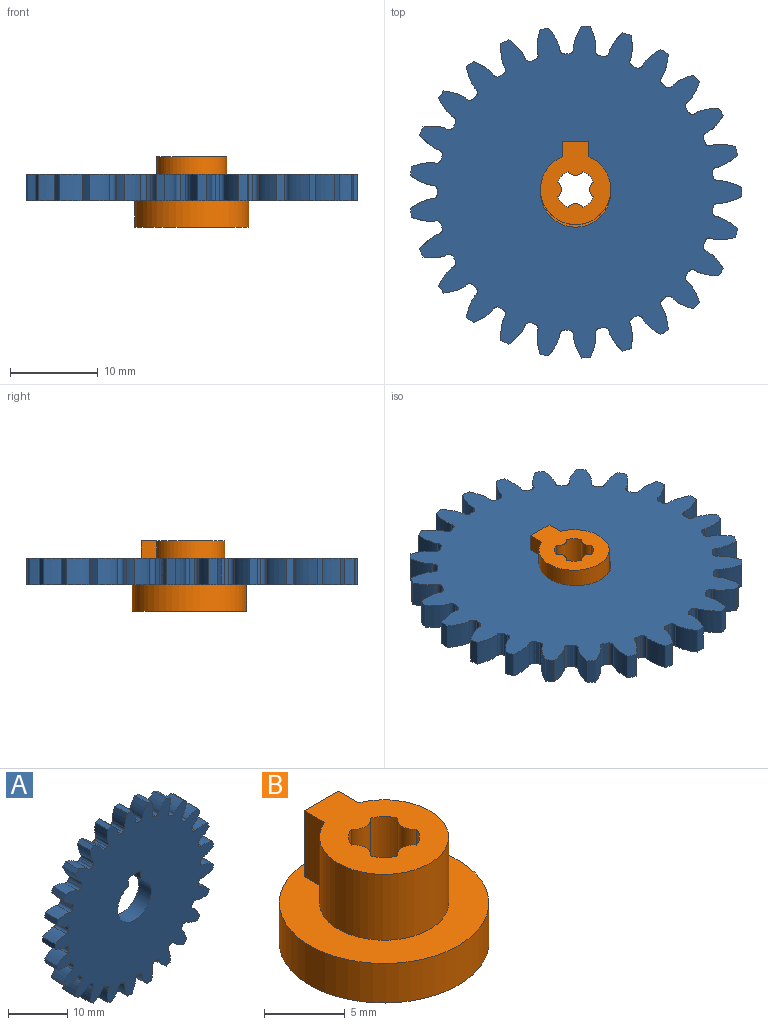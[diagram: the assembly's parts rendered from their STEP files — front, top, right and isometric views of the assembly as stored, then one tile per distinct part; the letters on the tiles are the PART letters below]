
ASSEMBLY  parts=2 mates=1
PART A: 156 faces, bbox 37.7x3x37.8 mm
  f0: cylinder r=18.9mm len=3mm, axis (0,1,0), area 3mm2, adj f24,f30,f141,f153
  f1: cylinder r=18.9mm len=3mm, axis (0,1,0), area 3mm2, adj f24,f30,f148,f151
  f2: cylinder r=18.9mm len=3mm, axis (0,1,0), area 3mm2, adj f24,f30,f136,f143
  f3: cylinder r=18.9mm len=3mm, axis (0,1,0), area 3mm2, adj f24,f30,f131,f138
  f4: cylinder r=18.9mm len=3mm, axis (0,1,0), area 3mm2, adj f24,f30,f126,f133
  f5: cylinder r=18.9mm len=3mm, axis (0,1,0), area 3mm2, adj f24,f30,f116,f128
  f6: cylinder r=18.9mm len=3mm, axis (0,1,0), area 3mm2, adj f24,f30,f111,f123
  f7: cylinder r=18.9mm len=3mm, axis (0,1,0), area 3mm2, adj f24,f30,f118,f121
  f8: cylinder r=18.9mm len=3mm, axis (0,1,0), area 3mm2, adj f24,f30,f106,f113
  f9: cylinder r=18.9mm len=3mm, axis (0,1,0), area 3mm2, adj f24,f30,f101,f108
  f10: cylinder r=18.9mm len=3mm, axis (0,1,0), area 3mm2, adj f24,f30,f96,f103
  f11: cylinder r=18.9mm len=3mm, axis (0,1,0), area 3mm2, adj f24,f30,f81,f98
  f12: cylinder r=18.9mm len=3mm, axis (0,1,0), area 3mm2, adj f24,f30,f31,f93
  f13: cylinder r=18.9mm len=3mm, axis (0,1,0), area 3mm2, adj f24,f30,f88,f91
  f14: cylinder r=18.9mm len=3mm, axis (0,1,0), area 3mm2, adj f24,f30,f76,f83
  f15: cylinder r=18.9mm len=3mm, axis (0,1,0), area 3mm2, adj f24,f30,f78,f86
  f16: cylinder r=18.9mm len=3mm, axis (0,1,0), area 3mm2, adj f24,f30,f73,f146
  f17: cylinder r=18.9mm len=3mm, axis (0,1,0), area 3mm2, adj f24,f30,f68,f71
  f18: cylinder r=18.9mm len=3mm, axis (0,1,0), area 3mm2, adj f24,f30,f63,f66
  f19: cylinder r=18.9mm len=3mm, axis (0,1,0), area 3mm2, adj f24,f30,f58,f61
  f20: cylinder r=18.9mm len=3mm, axis (0,1,0), area 3mm2, adj f24,f30,f46,f53
  f21: cylinder r=18.9mm len=3mm, axis (0,1,0), area 3mm2, adj f24,f30,f36,f48
  f22: cylinder r=18.9mm len=3mm, axis (0,1,0), area 3mm2, adj f24,f30,f43,f56
  f23: cylinder r=18.9mm len=3mm, axis (0,1,0), area 3mm2, adj f24,f30,f38,f41
  f24: plane 37.78x37.71mm, normal (0,-1,0), area 892.9mm2, adj f0,f1,f2,f3,f4,f5,f6,f7
  f25: plane 3x1.79mm, normal (-1,0,0), area 5.4mm2, adj f24,f26,f28,f30
  f26: cylinder r=4mm len=8mm, axis (0,1,0), area 66.2mm2, adj f24,f25,f27,f30
  f27: plane 3x1.79mm, normal (1,0,0), area 5.4mm2, adj f24,f26,f28,f30
  f28: plane 3x3mm, normal (0,0,-1), area 9mm2, adj f24,f25,f27,f30
  f29: cylinder r=18.9mm len=3mm, axis (0,1,0), area 3mm2, adj f24,f30,f33,f51
  f30: plane 37.78x37.71mm, normal (0,1,0), area 892.9mm2, adj f0,f1,f2,f3,f4,f5,f6,f7
  f31: extruded ~3x2.56mm, area 8.4mm2, adj f12,f24,f30,f34
  f32: cylinder r=15.75mm len=3mm, axis (0,1,0), area 1.4mm2, adj f24,f30,f34,f35
  f33: extruded ~3x2.56mm, area 8.4mm2, adj f24,f29,f30,f35
  f34: cylinder r=0.53mm len=3mm, axis (0,1,0), area 2.4mm2, adj f24,f30,f31,f32
  f35: cylinder r=0.53mm len=3mm, axis (0,1,0), area 2.4mm2, adj f24,f30,f32,f33
  f36: extruded ~3x2.61mm, area 8.4mm2, adj f21,f24,f30,f39
  f37: cylinder r=15.75mm len=3mm, axis (0,1,0), area 1.4mm2, adj f24,f30,f39,f40
  f38: extruded ~3x2.54mm, area 8.4mm2, adj f23,f24,f30,f40
  f39: cylinder r=0.53mm len=3mm, axis (0,1,0), area 2.4mm2, adj f24,f30,f36,f37
  f40: cylinder r=0.53mm len=3mm, axis (0,1,0), area 2.4mm2, adj f24,f30,f37,f38
  f41: extruded ~3x2.29mm, area 8.4mm2, adj f23,f24,f30,f44
  f42: cylinder r=15.75mm len=3mm, axis (0,1,0), area 1.4mm2, adj f24,f30,f44,f45
  f43: extruded ~3x2.74mm, area 8.4mm2, adj f22,f24,f30,f45
  f44: cylinder r=0.53mm len=3mm, axis (0,1,0), area 2.4mm2, adj f24,f30,f41,f42
  f45: cylinder r=0.53mm len=3mm, axis (0,1,0), area 2.4mm2, adj f24,f30,f42,f43
  f46: extruded ~3x2.77mm, area 8.4mm2, adj f20,f24,f30,f49
  f47: cylinder r=15.75mm len=3mm, axis (0,1,0), area 1.4mm2, adj f24,f30,f49,f50
  f48: extruded ~3x2.19mm, area 8.4mm2, adj f21,f24,f30,f50
  f49: cylinder r=0.53mm len=3mm, axis (0,1,0), area 2.4mm2, adj f24,f30,f46,f47
  f50: cylinder r=0.53mm len=3mm, axis (0,1,0), area 2.4mm2, adj f24,f30,f47,f48
  f51: extruded ~3x2.75mm, area 8.4mm2, adj f24,f29,f30,f54
  f52: cylinder r=15.75mm len=3mm, axis (0,1,0), area 1.4mm2, adj f24,f30,f54,f55
  f53: extruded ~3x2.2mm, area 8.4mm2, adj f20,f24,f30,f55
  f54: cylinder r=0.53mm len=3mm, axis (0,1,0), area 2.4mm2, adj f24,f30,f51,f52
  f55: cylinder r=0.53mm len=3mm, axis (0,1,0), area 2.4mm2, adj f24,f30,f52,f53
  f56: extruded ~3x2.09mm, area 8.4mm2, adj f22,f24,f30,f59
  f57: cylinder r=15.75mm len=3mm, axis (0,1,0), area 1.4mm2, adj f24,f30,f59,f60
  f58: extruded ~3x2.77mm, area 8.4mm2, adj f19,f24,f30,f60
  f59: cylinder r=0.53mm len=3mm, axis (0,1,0), area 2.4mm2, adj f24,f30,f56,f57
  f60: cylinder r=0.53mm len=3mm, axis (0,1,0), area 2.4mm2, adj f24,f30,f57,f58
  f61: extruded ~3x2.48mm, area 8.4mm2, adj f19,f24,f30,f64
  f62: cylinder r=15.75mm len=3mm, axis (0,1,0), area 1.4mm2, adj f24,f30,f64,f65
  f63: extruded ~3x2.62mm, area 8.4mm2, adj f18,f24,f30,f65
  f64: cylinder r=0.53mm len=3mm, axis (0,1,0), area 2.4mm2, adj f24,f30,f61,f62
  f65: cylinder r=0.53mm len=3mm, axis (0,1,0), area 2.4mm2, adj f24,f30,f62,f63
  f66: extruded ~3x2.71mm, area 8.4mm2, adj f18,f24,f30,f69
  f67: cylinder r=15.75mm len=3mm, axis (0,1,0), area 1.4mm2, adj f24,f30,f69,f70
  f68: extruded ~3x2.31mm, area 8.4mm2, adj f17,f24,f30,f70
  f69: cylinder r=0.53mm len=3mm, axis (0,1,0), area 2.4mm2, adj f24,f30,f66,f67
  f70: cylinder r=0.53mm len=3mm, axis (0,1,0), area 2.4mm2, adj f24,f30,f67,f68
  f71: extruded ~3x2.78mm, area 8.4mm2, adj f17,f24,f30,f74
  f72: cylinder r=15.75mm len=3mm, axis (0,1,0), area 1.4mm2, adj f24,f30,f74,f75
  f73: extruded ~3x2.08mm, area 8.4mm2, adj f16,f24,f30,f75
  f74: cylinder r=0.53mm len=3mm, axis (0,1,0), area 2.4mm2, adj f24,f30,f71,f72
  f75: cylinder r=0.53mm len=3mm, axis (0,1,0), area 2.4mm2, adj f24,f30,f72,f73
  f76: extruded ~3x2.54mm, area 8.4mm2, adj f14,f24,f30,f79
  f77: cylinder r=15.75mm len=3mm, axis (0,1,0), area 1.4mm2, adj f24,f30,f79,f80
  f78: extruded ~3x2.61mm, area 8.4mm2, adj f15,f24,f30,f80
  f79: cylinder r=0.53mm len=3mm, axis (0,1,0), area 2.4mm2, adj f24,f30,f76,f77
  f80: cylinder r=0.53mm len=3mm, axis (0,1,0), area 2.4mm2, adj f24,f30,f77,f78
  f81: extruded ~3x2.74mm, area 8.4mm2, adj f11,f24,f30,f84
  f82: cylinder r=15.75mm len=3mm, axis (0,1,0), area 1.4mm2, adj f24,f30,f84,f85
  f83: extruded ~3x2.29mm, area 8.4mm2, adj f14,f24,f30,f85
  f84: cylinder r=0.53mm len=3mm, axis (0,1,0), area 2.4mm2, adj f24,f30,f81,f82
  f85: cylinder r=0.53mm len=3mm, axis (0,1,0), area 2.4mm2, adj f24,f30,f82,f83
  f86: extruded ~3x2.19mm, area 8.4mm2, adj f15,f24,f30,f89
  f87: cylinder r=15.75mm len=3mm, axis (0,1,0), area 1.4mm2, adj f24,f30,f89,f90
  f88: extruded ~3x2.77mm, area 8.4mm2, adj f13,f24,f30,f90
  f89: cylinder r=0.53mm len=3mm, axis (0,1,0), area 2.4mm2, adj f24,f30,f86,f87
  f90: cylinder r=0.53mm len=3mm, axis (0,1,0), area 2.4mm2, adj f24,f30,f87,f88
  f91: extruded ~3x2.2mm, area 8.4mm2, adj f13,f24,f30,f94
  f92: cylinder r=15.75mm len=3mm, axis (0,1,0), area 1.4mm2, adj f24,f30,f94,f95
  f93: extruded ~3x2.75mm, area 8.4mm2, adj f12,f24,f30,f95
  f94: cylinder r=0.53mm len=3mm, axis (0,1,0), area 2.4mm2, adj f24,f30,f91,f92
  f95: cylinder r=0.53mm len=3mm, axis (0,1,0), area 2.4mm2, adj f24,f30,f92,f93
  f96: extruded ~3x2.77mm, area 8.4mm2, adj f10,f24,f30,f99
  f97: cylinder r=15.75mm len=3mm, axis (0,1,0), area 1.4mm2, adj f24,f30,f99,f100
  f98: extruded ~3x2.09mm, area 8.4mm2, adj f11,f24,f30,f100
  f99: cylinder r=0.53mm len=3mm, axis (0,1,0), area 2.4mm2, adj f24,f30,f96,f97
  f100: cylinder r=0.53mm len=3mm, axis (0,1,0), area 2.4mm2, adj f24,f30,f97,f98
  f101: extruded ~3x2.62mm, area 8.4mm2, adj f9,f24,f30,f104
  f102: cylinder r=15.75mm len=3mm, axis (0,1,0), area 1.4mm2, adj f24,f30,f104,f105
  f103: extruded ~3x2.48mm, area 8.4mm2, adj f10,f24,f30,f105
  f104: cylinder r=0.53mm len=3mm, axis (0,1,0), area 2.4mm2, adj f24,f30,f101,f102
  f105: cylinder r=0.53mm len=3mm, axis (0,1,0), area 2.4mm2, adj f24,f30,f102,f103
  f106: extruded ~3x2.31mm, area 8.4mm2, adj f8,f24,f30,f109
  f107: cylinder r=15.75mm len=3mm, axis (0,1,0), area 1.4mm2, adj f24,f30,f109,f110
  f108: extruded ~3x2.71mm, area 8.4mm2, adj f9,f24,f30,f110
  f109: cylinder r=0.53mm len=3mm, axis (0,1,0), area 2.4mm2, adj f24,f30,f106,f107
  f110: cylinder r=0.53mm len=3mm, axis (0,1,0), area 2.4mm2, adj f24,f30,f107,f108
  f111: extruded ~3x2.08mm, area 8.4mm2, adj f6,f24,f30,f114
  f112: cylinder r=15.75mm len=3mm, axis (0,1,0), area 1.4mm2, adj f24,f30,f114,f115
  f113: extruded ~3x2.78mm, area 8.4mm2, adj f8,f24,f30,f115
  f114: cylinder r=0.53mm len=3mm, axis (0,1,0), area 2.4mm2, adj f24,f30,f111,f112
  f115: cylinder r=0.53mm len=3mm, axis (0,1,0), area 2.4mm2, adj f24,f30,f112,f113
  f116: extruded ~3x2.71mm, area 8.4mm2, adj f5,f24,f30,f119
  f117: cylinder r=15.75mm len=3mm, axis (0,1,0), area 1.4mm2, adj f24,f30,f119,f120
  f118: extruded ~3x2.38mm, area 8.4mm2, adj f7,f24,f30,f120
  f119: cylinder r=0.53mm len=3mm, axis (0,1,0), area 2.4mm2, adj f24,f30,f116,f117
  f120: cylinder r=0.53mm len=3mm, axis (0,1,0), area 2.4mm2, adj f24,f30,f117,f118
  f121: extruded ~3x2.47mm, area 8.4mm2, adj f7,f24,f30,f124
  f122: cylinder r=15.75mm len=3mm, axis (0,1,0), area 1.4mm2, adj f24,f30,f124,f125
  f123: extruded ~3x2.66mm, area 8.4mm2, adj f6,f24,f30,f125
  f124: cylinder r=0.53mm len=3mm, axis (0,1,0), area 2.4mm2, adj f24,f30,f121,f122
  f125: cylinder r=0.53mm len=3mm, axis (0,1,0), area 2.4mm2, adj f24,f30,f122,f123
  f126: extruded ~3x2.78mm, area 8.4mm2, adj f4,f24,f30,f129
  f127: cylinder r=15.75mm len=3mm, axis (0,1,0), area 1.4mm2, adj f24,f30,f129,f130
  f128: extruded ~3x1.97mm, area 8.4mm2, adj f5,f24,f30,f130
  f129: cylinder r=0.53mm len=3mm, axis (0,1,0), area 2.4mm2, adj f24,f30,f126,f127
  f130: cylinder r=0.53mm len=3mm, axis (0,1,0), area 2.4mm2, adj f24,f30,f127,f128
  f131: extruded ~3x2.67mm, area 8.4mm2, adj f3,f24,f30,f134
  f132: cylinder r=15.75mm len=3mm, axis (0,1,0), area 1.4mm2, adj f24,f30,f134,f135
  f133: extruded ~3x2.4mm, area 8.4mm2, adj f4,f24,f30,f135
  f134: cylinder r=0.53mm len=3mm, axis (0,1,0), area 2.4mm2, adj f24,f30,f131,f132
  f135: cylinder r=0.53mm len=3mm, axis (0,1,0), area 2.4mm2, adj f24,f30,f132,f133
  f136: extruded ~3x2.4mm, area 8.4mm2, adj f2,f24,f30,f139
  f137: cylinder r=15.75mm len=3mm, axis (0,1,0), area 1.4mm2, adj f24,f30,f139,f140
  f138: extruded ~3x2.67mm, area 8.4mm2, adj f3,f24,f30,f140
  f139: cylinder r=0.53mm len=3mm, axis (0,1,0), area 2.4mm2, adj f24,f30,f136,f137
  f140: cylinder r=0.53mm len=3mm, axis (0,1,0), area 2.4mm2, adj f24,f30,f137,f138
  f141: extruded ~3x1.97mm, area 8.4mm2, adj f0,f24,f30,f144
  f142: cylinder r=15.75mm len=3mm, axis (0,1,0), area 1.4mm2, adj f24,f30,f144,f145
  f143: extruded ~3x2.78mm, area 8.4mm2, adj f2,f24,f30,f145
  f144: cylinder r=0.53mm len=3mm, axis (0,1,0), area 2.4mm2, adj f24,f30,f141,f142
  f145: cylinder r=0.53mm len=3mm, axis (0,1,0), area 2.4mm2, adj f24,f30,f142,f143
  f146: extruded ~3x2.66mm, area 8.4mm2, adj f16,f24,f30,f149
  f147: cylinder r=15.75mm len=3mm, axis (0,1,0), area 1.4mm2, adj f24,f30,f149,f150
  f148: extruded ~3x2.47mm, area 8.4mm2, adj f1,f24,f30,f150
  f149: cylinder r=0.53mm len=3mm, axis (0,1,0), area 2.4mm2, adj f24,f30,f146,f147
  f150: cylinder r=0.53mm len=3mm, axis (0,1,0), area 2.4mm2, adj f24,f30,f147,f148
  f151: extruded ~3x2.38mm, area 8.4mm2, adj f1,f24,f30,f154
  f152: cylinder r=15.75mm len=3mm, axis (0,1,0), area 1.4mm2, adj f24,f30,f154,f155
  f153: extruded ~3x2.71mm, area 8.4mm2, adj f0,f24,f30,f155
  f154: cylinder r=0.53mm len=3mm, axis (0,1,0), area 2.4mm2, adj f24,f30,f151,f152
  f155: cylinder r=0.53mm len=3mm, axis (0,1,0), area 2.4mm2, adj f24,f30,f152,f153
PART B: 18 faces, bbox 13x13x8 mm
  f0: cylinder r=2.2mm len=6mm, axis (0,0,-1), area 10.6mm2, adj f11,f13,f14,f17
  f1: cylinder r=2.2mm len=6mm, axis (0,0,-1), area 10.6mm2, adj f11,f13,f16,f17
  f2: cylinder r=2.2mm len=6mm, axis (0,0,-1), area 10.6mm2, adj f11,f13,f15,f16
  f3: cylinder r=2.2mm len=6mm, axis (0,0,-1), area 10.6mm2, adj f11,f13,f14,f15
  f4: cylinder r=6.5mm len=13mm, axis (0,0,-1), area 122.5mm2, adj f5,f6
  f5: plane 13x13mm, normal (0,0,1), area 77.7mm2, adj f4,f7,f8,f9,f10
  f6: plane 13x13mm, normal (0,0,-1), area 99.5mm2, adj f4,f12
  f7: cylinder r=4mm len=8mm, axis (0,0,-1), area 110.3mm2, adj f5,f8,f10,f11
  f8: plane 5x1.79mm, normal (1,0,0), area 9mm2, adj f5,f7,f9,f11
  f9: plane 5x3mm, normal (0,1,0), area 15mm2, adj f5,f8,f10,f11
  f10: plane 5x1.79mm, normal (-1,0,0), area 9mm2, adj f5,f7,f9,f11
  f11: plane 9.5x8mm, normal (0,0,1), area 42.6mm2, adj f0,f1,f2,f3,f7,f8,f9,f10
  f12: cylinder r=3.25mm len=6.5mm, axis (0,0,1), area 40.8mm2, adj f6,f13
  f13: plane 6.5x6.5mm, normal (0,0,-1), area 20.7mm2, adj f0,f1,f2,f3,f12,f14,f15,f16
  f14: cylinder r=1mm len=6mm, axis (0,0,1), area 11.7mm2, adj f0,f3,f11,f13
  f15: cylinder r=1mm len=6mm, axis (0,0,1), area 11.7mm2, adj f2,f3,f11,f13
  f16: cylinder r=1mm len=6mm, axis (0,0,1), area 11.7mm2, adj f1,f2,f11,f13
  f17: cylinder r=1mm len=6mm, axis (0,0,1), area 11.7mm2, adj f0,f1,f11,f13
PLACE A rot(axis=(0,0.71,0.71),180deg) t=(10.96,11.65,10.41)mm
PLACE B t=(10.96,11.94,-9.59)mm
MATE fastened A.f0 <-> B.f5  axis (0,0,-1) through (10.96,11.65,7.41)mm
